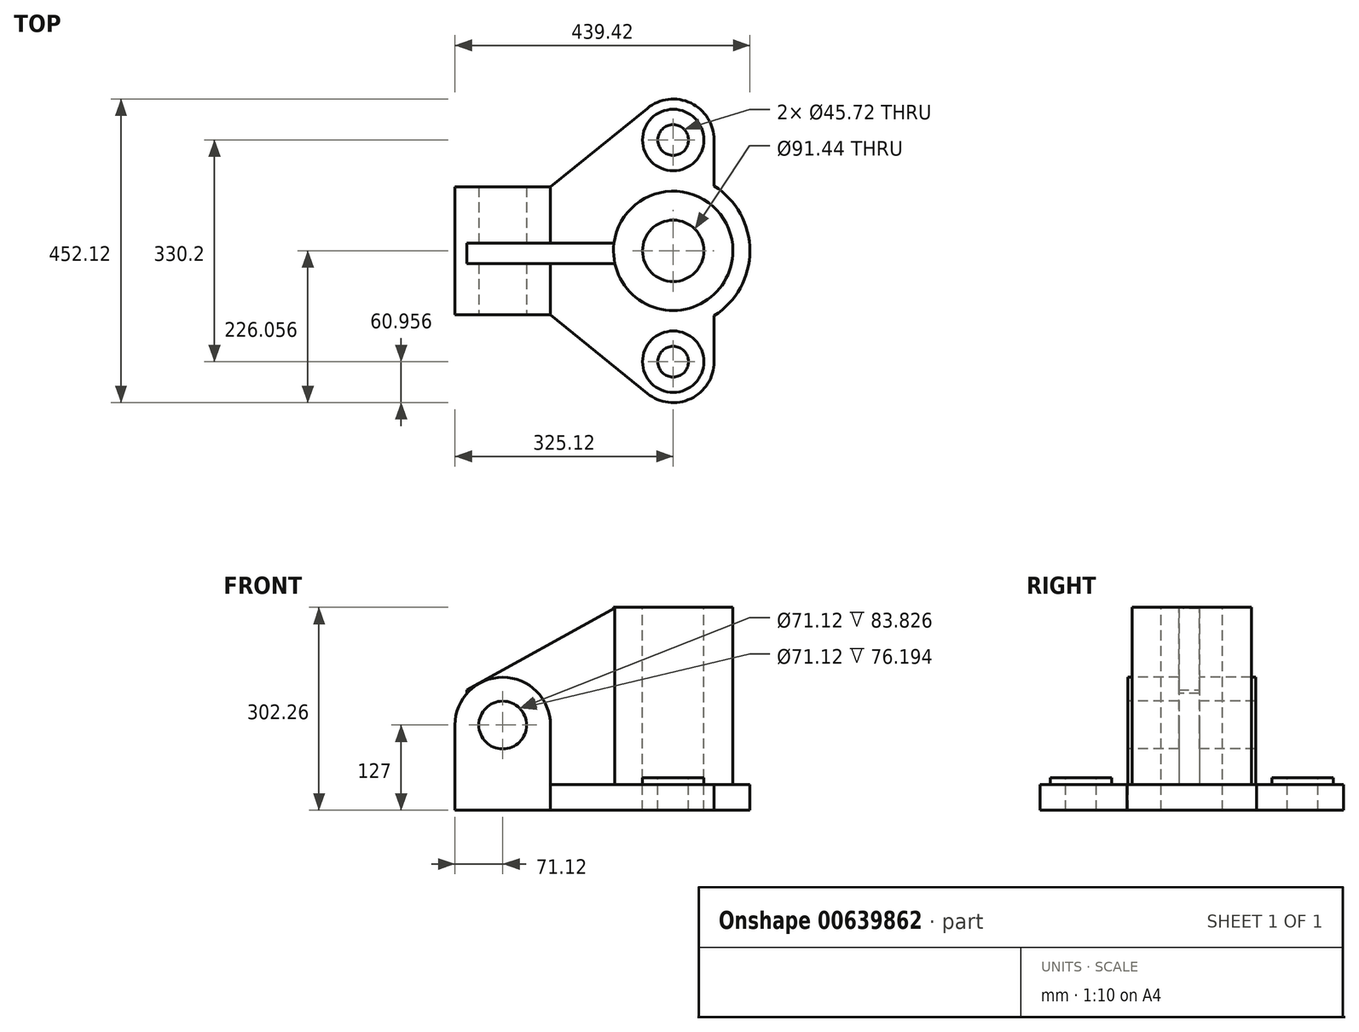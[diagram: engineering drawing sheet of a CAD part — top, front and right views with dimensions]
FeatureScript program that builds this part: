
annotation { "Feature Type Name" : "Feature", "Feature Type Description" : "" }
export const myFeature = defineFeature(function(context is Context, id is Id, definition is map)
    precondition{}
    {
        {
            var Q0;
            Q0=qCreatedBy(makeId("Top.planeOp"),FACE);
            var sketch = newSketch(context, id + "F0", { "sketchPlane" : qUnion([Q0])});
            skLineSegment(sketch, "E0.bottom", {"start": v(-196, 83.83) * mm, "end": v(-53.76, 83.83) * mm});
            skLineSegment(sketch, "E0.top", {"start": v(-196, -106.67) * mm, "end": v(-53.76, -106.67) * mm});
            skLineSegment(sketch, "E0.left", {"start": v(-196, 83.83) * mm, "end": v(-196, -106.67) * mm});
            skLineSegment(sketch, "E0.right", {"start": v(-53.76, 83.83) * mm, "end": v(-53.76, -106.67) * mm});
            skLineSegment(sketch, "E1", {"start": v(-53.76, 83.83) * mm, "end": v(90.72, 201.02) * mm});
            skArc(sketch, "E2", {"start": v(90.72, 201.02) * mm, "mid": v(155.34, 208.7) * mm, "end": v(190.08, 153.68) * mm});
            skLineSegment(sketch, "E3", {"start": v(190.08, 153.68) * mm, "end": v(190.08, 85.26) * mm});
            skArc(sketch, "E4", {"start": v(190.08, -108.11) * mm, "mid": v(243.42, -11.42) * mm, "end": v(190.08, 85.26) * mm});
            skLineSegment(sketch, "E5", {"start": v(190.08, -108.11) * mm, "end": v(190.08, -176.52) * mm});
            skArc(sketch, "E6", {"start": v(190.08, -176.52) * mm, "mid": v(155.34, -231.56) * mm, "end": v(90.72, -223.87) * mm});
            skLineSegment(sketch, "E7", {"start": v(90.72, -223.87) * mm, "end": v(-53.76, -106.67) * mm});
            skSolve(sketch);
        }
        {
            var Q0;
            Q0=makeQuery(id+"F0.imprint","IMPRINT",FACE,{"disambiguationData":[TD([[makeQuery(id+"F0.imprint","IMPRINT",EDGE,{"derivedFrom":sQuery(id+"F0.wireOp",EDGE,"E0.right")}),1.0]])]});
            extrude(context, id + "F1", {"entities" : qUnion([Q0]), "depth" : 38.1 * mm, "offsetDistance" : 25.4 * mm});
        }
        {
            var Q0;
            Q0=makeQuery(id+"F0.imprint","IMPRINT",FACE,{"disambiguationData":[TD([[makeQuery(id+"F0.imprint","IMPRINT",EDGE,{"derivedFrom":sQuery(id+"F0.wireOp",EDGE,"E0.bottom")}),-1.0]])]});
            extrude(context, id + "F2", {"entities" : qUnion([Q0]), "operationType" : NewBodyOperationType.ADD, "depth" : 127 * mm, "offsetDistance" : 25.4 * mm});
        }
        {
            var Q0;
            Q0=makeQuery(id+"F2.opExtrude","SWEPT_FACE",FACE,{"disambiguationData":[OSD([sQuery(id+"F0.wireOp",EDGE,"E0.top")])]});
            var sketch = newSketch(context, id + "F3", { "sketchPlane" : qUnion([Q0])});
            skCircle(sketch, "E8", {"center": v(-124.88, 127) * mm, "radius": 71.12 * mm});
            skSolve(sketch);
        }
        {
            var Q0;
            {var subQ1=sQuery(id+"F0.wireOp",EDGE,"E0.top");var subQ2=makeQuery(id+"F2.opExtrude","CAP_EDGE",EDGE,{"disambiguationData":[OSD([subQ1])],"isStart":false});Q0=makeQuery(id+"F3.imprint","IMPRINT",FACE,{"disambiguationData":[TD([[makeQuery(id+"F3.imprint","IMPRINT",EDGE,{"derivedFrom":subQ2}),1.0]])]});}
            extrude(context, id + "F4", {"entities" : qUnion([Q0]), "operationType" : NewBodyOperationType.ADD, "oppositeDirection" : true, "depth" : 190.5 * mm, "offsetDistance" : 190.5 * mm});
        }
        {
            var Q0;
            {var subQ0=sQuery(id+"F0.wireOp",EDGE,"E0.top");Q0=makeQuery(id+"F4.boolean.opBoolean","MERGE",FACE,{"derivedFrom":[makeQuery(id+"F2.opExtrude","SWEPT_FACE",FACE,{"disambiguationData":[OSD([subQ0])]}),makeQuery(id+"F4.opExtrude","CAP_FACE",FACE,{"disambiguationData":[OSD([subQ0,sQuery(id+"F3.wireOp",EDGE,"E8")])],"isStart":true})]});}
            var sketch = newSketch(context, id + "F5", { "sketchPlane" : qUnion([Q0])});
            skCircle(sketch, "E9", {"center": v(-124.88, 127) * mm, "radius": 35.56 * mm});
            skSolve(sketch);
        }
        {
            var Q0;
            Q0 = qSketchRegion(id + "F5", true);
            extrude(context, id + "F6", {"entities" : qUnion([Q0]), "operationType" : NewBodyOperationType.REMOVE, "oppositeDirection" : true, "depth" : 190.5 * mm, "offsetDistance" : 25.4 * mm});
        }
        {
            var Q0;
            Q0=makeQuery(id+"F1.opExtrude","CAP_FACE",FACE,{"disambiguationData":[OSD([sQuery(id+"F0.wireOp",EDGE,"E0.right"),sQuery(id+"F0.wireOp",EDGE,"E1"),sQuery(id+"F0.wireOp",EDGE,"E2"),sQuery(id+"F0.wireOp",EDGE,"E3"),sQuery(id+"F0.wireOp",EDGE,"E4"),sQuery(id+"F0.wireOp",EDGE,"E5"),sQuery(id+"F0.wireOp",EDGE,"E6"),sQuery(id+"F0.wireOp",EDGE,"E7")])],"isStart":false});
            var sketch = newSketch(context, id + "F7", { "sketchPlane" : qUnion([Q0])});
            skCircle(sketch, "E10", {"center": v(129.12, 153.68) * mm, "radius": 45.72 * mm});
            skCircle(sketch, "E11", {"center": v(129.12, -176.52) * mm, "radius": 45.72 * mm});
            skSolve(sketch);
        }
        {
            var Q0;
            Q0=makeQuery(id+"F7.imprint","IMPRINT",FACE,{"disambiguationData":[TD([[makeQuery(id+"F7.imprint","IMPRINT",EDGE,{"derivedFrom":sQuery(id+"F7.wireOp",EDGE,"E11")}),1.0]])]});
            extrude(context, id + "F8", {"entities" : qUnion([Q0]), "operationType" : NewBodyOperationType.ADD, "depth" : 10.16 * mm, "offsetDistance" : 25.4 * mm});
        }
        {
            var Q0;
            Q0 = qSketchRegion(id + "F7", true);
            var Q1;
            Q1=sQuery(id+"F7.wireOp",EDGE,"E10");
            extrude(context, id + "F9", {"entities" : qUnion([Q0]), "operationType" : NewBodyOperationType.ADD, "surfaceEntities" : qUnion([Q1]), "depth" : 10.16 * mm, "offsetDistance" : 25.4 * mm});
        }
        {
            var Q0;
            Q0=makeQuery(id+"F9.opExtrude","CAP_FACE",FACE,{"disambiguationData":[OSD([sQuery(id+"F7.wireOp",EDGE,"E10")])],"isStart":false});
            var sketch = newSketch(context, id + "F10", { "sketchPlane" : qUnion([Q0])});
            skCircle(sketch, "E12", {"center": v(129.12, 153.68) * mm, "radius": 22.86 * mm});
            skSolve(sketch);
        }
        {
            var Q0;
            Q0 = qSketchRegion(id + "F10", true);
            extrude(context, id + "F11", {"entities" : qUnion([Q0]), "operationType" : NewBodyOperationType.REMOVE, "oppositeDirection" : true, "depth" : 48.26 * mm, "offsetDistance" : 25.4 * mm});
        }
        {
            var Q0;
            Q0=makeQuery(id+"F8.opExtrude","CAP_FACE",FACE,{"disambiguationData":[OSD([sQuery(id+"F7.wireOp",EDGE,"E11")])],"isStart":false});
            var sketch = newSketch(context, id + "F12", { "sketchPlane" : qUnion([Q0])});
            skCircle(sketch, "E13", {"center": v(129.12, -176.52) * mm, "radius": 22.86 * mm});
            skSolve(sketch);
        }
        {
            var Q0;
            Q0 = qSketchRegion(id + "F12", true);
            extrude(context, id + "F13", {"entities" : qUnion([Q0]), "operationType" : NewBodyOperationType.REMOVE, "oppositeDirection" : true, "depth" : 48.26 * mm, "offsetDistance" : 25.4 * mm});
        }
        {
            var Q0;
            Q0=makeQuery(id+"F1.opExtrude","CAP_FACE",FACE,{"disambiguationData":[OSD([sQuery(id+"F0.wireOp",EDGE,"E0.right"),sQuery(id+"F0.wireOp",EDGE,"E1"),sQuery(id+"F0.wireOp",EDGE,"E2"),sQuery(id+"F0.wireOp",EDGE,"E3"),sQuery(id+"F0.wireOp",EDGE,"E4"),sQuery(id+"F0.wireOp",EDGE,"E5"),sQuery(id+"F0.wireOp",EDGE,"E6"),sQuery(id+"F0.wireOp",EDGE,"E7")])],"isStart":false});
            var sketch = newSketch(context, id + "F14", { "sketchPlane" : qUnion([Q0])});
            skCircle(sketch, "E14", {"center": v(129.12, -11.42) * mm, "radius": 88.9 * mm});
            skSolve(sketch);
        }
        {
            var Q0;
            Q0 = qSketchRegion(id + "F14", true);
            extrude(context, id + "F15", {"entities" : qUnion([Q0]), "operationType" : NewBodyOperationType.ADD, "depth" : 264.16 * mm, "offsetDistance" : 25.4 * mm});
        }
        {
            var Q0;
            Q0=makeQuery(id+"F15.opExtrude","CAP_FACE",FACE,{"disambiguationData":[OSD([sQuery(id+"F14.wireOp",EDGE,"E14")])],"isStart":false});
            var sketch = newSketch(context, id + "F16", { "sketchPlane" : qUnion([Q0])});
            skCircle(sketch, "E15", {"center": v(129.12, -11.42) * mm, "radius": 45.72 * mm});
            skSolve(sketch);
        }
        {
            var Q0;
            Q0 = qSketchRegion(id + "F16", true);
            extrude(context, id + "F17", {"entities" : qUnion([Q0]), "operationType" : NewBodyOperationType.REMOVE, "oppositeDirection" : true, "depth" : 302.26 * mm, "offsetDistance" : 25.4 * mm});
        }
        {
            var Q0;
            Q0=qCreatedBy(makeId("Front.planeOp"),FACE);
            var sketch = newSketch(context, id + "F18", { "sketchPlane" : qUnion([Q0])});
            skLineSegment(sketch, "E16", {"start": v(-178.07, 179.18) * mm, "end": v(43.6, 302.26) * mm});
            skLineSegment(sketch, "E17", {"start": v(43.6, 302.26) * mm, "end": v(43.6, 0) * mm});
            skLineSegment(sketch, "E18", {"start": v(43.6, 0) * mm, "end": v(-178.07, 0) * mm});
            skLineSegment(sketch, "E19", {"start": v(-178.07, 179.18) * mm, "end": v(-178.07, 0) * mm});
            skLineSegment(sketch, "E20", {"start": v(-178.07, 0) * mm, "end": v(43.6, 0) * mm});
            skSolve(sketch);
        }
        {
            var Q0;
            Q0=makeQuery(id+"F18.imprint","IMPRINT",FACE,{"disambiguationData":[TD([[makeQuery(id+"F18.imprint","IMPRINT",EDGE,{"derivedFrom":sQuery(id+"F18.wireOp",EDGE,"E16")}),-1.0]])]});
            extrude(context, id + "F19", {"entities" : qUnion([Q0]), "operationType" : NewBodyOperationType.ADD, "depth" : 30.48 * mm, "offsetDistance" : 25.4 * mm});
        }
    });
